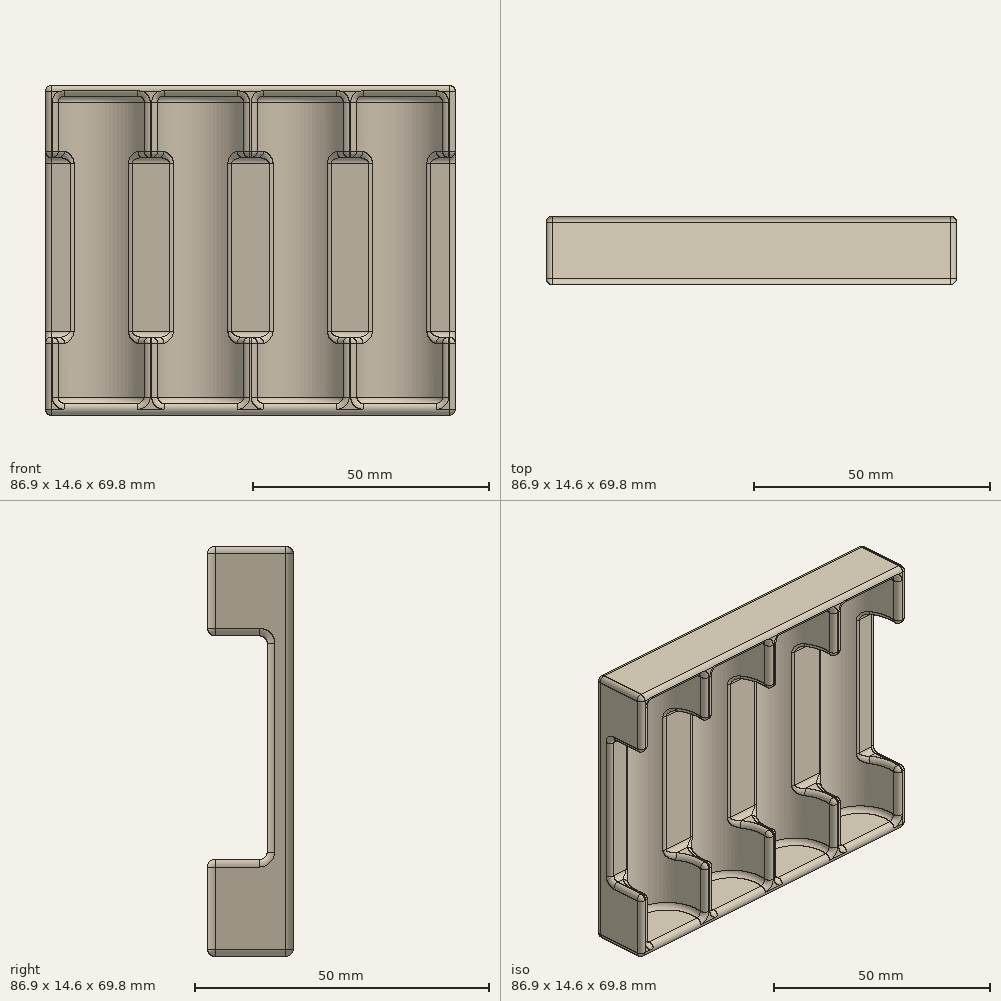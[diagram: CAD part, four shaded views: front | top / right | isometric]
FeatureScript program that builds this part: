
annotation { "Feature Type Name" : "Feature", "Feature Type Description" : "" }
export const myFeature = defineFeature(function(context is Context, id is Id, definition is map)
    precondition{}
    {
        {
            var Q0;
            Q0=qCreatedBy(makeId("Front.planeOp"),FACE);
            var sketch = newSketch(context, id + "F0", { "sketchPlane" : qUnion([Q0])});
            skLineSegment(sketch, "E0.bottom", {"start": v(0, 0) * mm, "end": v(86.87, 0) * mm});
            skLineSegment(sketch, "E0.top", {"start": v(0, 69.85) * mm, "end": v(86.87, 69.85) * mm});
            skLineSegment(sketch, "E0.left", {"start": v(0, 0) * mm, "end": v(0, 69.85) * mm});
            skLineSegment(sketch, "E0.right", {"start": v(86.87, 0) * mm, "end": v(86.87, 69.85) * mm});
            skSolve(sketch);
        }
        {
            var Q0;
            Q0=makeQuery(id+"F0.imprint","IMPRINT",FACE,{"disambiguationData":[TD([[makeQuery(id+"F0.imprint","IMPRINT",EDGE,{"derivedFrom":sQuery(id+"F0.wireOp",EDGE,"E0.bottom")}),1.0]])]});
            extrude(context, id + "F1", {"entities" : qUnion([Q0]), "depth" : 14.6 * mm});
        }
        {
            var Q0;
            Q0=makeQuery(id+"F1.opExtrude","SWEPT_FACE",FACE,{"disambiguationData":[OSD([sQuery(id+"F0.wireOp",EDGE,"E0.bottom")])]});
            var sketch = newSketch(context, id + "F2", { "sketchPlane" : qUnion([Q0])});
            skCircle(sketch, "E1", {"center": v(11.81, 11.43) * mm, "radius": 9.27 * mm});
            skCircle(sketch, "E2", {"center": v(32.9, 11.43) * mm, "radius": 9.27 * mm});
            skCircle(sketch, "E3", {"center": v(53.98, 11.43) * mm, "radius": 9.27 * mm});
            skCircle(sketch, "E4", {"center": v(75.06, 11.43) * mm, "radius": 9.27 * mm});
            skLineSegment(sketch, "E5", {"start": v(11.81, 11.43) * mm, "end": v(75.06, 11.43) * mm, "construction": true});
            skSolve(sketch);
        }
        {
            var Q0;
            {var subQ0=sQuery(id+"F2.wireOp",EDGE,"E1");var subQ1=makeQuery(id+"F1.opExtrude","CAP_EDGE",EDGE,{"disambiguationData":[OSD([sQuery(id+"F0.wireOp",EDGE,"E0.bottom")])],"isStart":false});var subQ2=makeQuery(id+"F2.imprint","INTERSECT",VERTEX,{"disambiguationData":[OD(0.0)],"derivedFrom":[subQ1,subQ0]});Q0=makeQuery(id+"F2.imprint","IMPRINT",FACE,{"disambiguationData":[TD([[makeQuery(id+"F2.imprint","IMPRINT",EDGE,{"disambiguationData":[TD([[subQ2,-1.0]])],"derivedFrom":subQ0}),1.0]])]});}
            var Q1;
            {var subQ0=sQuery(id+"F2.wireOp",EDGE,"E2");var subQ1=makeQuery(id+"F1.opExtrude","CAP_EDGE",EDGE,{"disambiguationData":[OSD([sQuery(id+"F0.wireOp",EDGE,"E0.bottom")])],"isStart":false});var subQ2=makeQuery(id+"F2.imprint","INTERSECT",VERTEX,{"disambiguationData":[OD(0.0)],"derivedFrom":[subQ1,subQ0]});Q1=makeQuery(id+"F2.imprint","IMPRINT",FACE,{"disambiguationData":[TD([[makeQuery(id+"F2.imprint","IMPRINT",EDGE,{"disambiguationData":[TD([[subQ2,-1.0]])],"derivedFrom":subQ0}),1.0]])]});}
            var Q2;
            {var subQ0=sQuery(id+"F2.wireOp",EDGE,"E3");var subQ1=makeQuery(id+"F1.opExtrude","CAP_EDGE",EDGE,{"disambiguationData":[OSD([sQuery(id+"F0.wireOp",EDGE,"E0.bottom")])],"isStart":false});var subQ2=makeQuery(id+"F2.imprint","INTERSECT",VERTEX,{"disambiguationData":[OD(0.0)],"derivedFrom":[subQ1,subQ0]});Q2=makeQuery(id+"F2.imprint","IMPRINT",FACE,{"disambiguationData":[TD([[makeQuery(id+"F2.imprint","IMPRINT",EDGE,{"disambiguationData":[TD([[subQ2,1.0]])],"derivedFrom":subQ0}),1.0]])]});}
            var Q3;
            {var subQ0=sQuery(id+"F2.wireOp",EDGE,"E4");var subQ1=makeQuery(id+"F1.opExtrude","CAP_EDGE",EDGE,{"disambiguationData":[OSD([sQuery(id+"F0.wireOp",EDGE,"E0.bottom")])],"isStart":false});var subQ2=makeQuery(id+"F2.imprint","INTERSECT",VERTEX,{"disambiguationData":[OD(0.0)],"derivedFrom":[subQ1,subQ0]});Q3=makeQuery(id+"F2.imprint","IMPRINT",FACE,{"disambiguationData":[TD([[makeQuery(id+"F2.imprint","IMPRINT",EDGE,{"disambiguationData":[TD([[subQ2,1.0]])],"derivedFrom":subQ0}),1.0]])]});}
            var Q4;
            Q4=sQuery(id+"F2.wireOp",EDGE,"E1");
            var Q5;
            Q5=sQuery(id+"F2.wireOp",EDGE,"E2");
            var Q6;
            Q6=sQuery(id+"F2.wireOp",EDGE,"E3");
            var Q7;
            Q7=sQuery(id+"F2.wireOp",EDGE,"E4");
            extrude(context, id + "F3", {"entities" : qUnion([Q0, Q1, Q2, Q3]), "operationType" : NewBodyOperationType.REMOVE, "surfaceEntities" : qUnion([Q4, Q5, Q6, Q7]), "oppositeDirection" : true, "depth" : 67.63 * mm, "hasSecondDirection" : true, "secondDirectionOppositeDirection" : true, "secondDirectionDepth" : 2.54 * mm});
        }
        {
            var Q0;
            Q0=makeQuery(id+"F1.opExtrude","CAP_FACE",FACE,{"disambiguationData":[OSD([sQuery(id+"F0.wireOp",EDGE,"E0.bottom"),sQuery(id+"F0.wireOp",EDGE,"E0.top"),sQuery(id+"F0.wireOp",EDGE,"E0.left"),sQuery(id+"F0.wireOp",EDGE,"E0.right")])],"isStart":false});
            var sketch = newSketch(context, id + "F4", { "sketchPlane" : qUnion([Q0])});
            skLineSegment(sketch, "E6.bottom", {"start": v(-1.4, 54.61) * mm, "end": v(92.29, 54.61) * mm});
            skLineSegment(sketch, "E6.top", {"start": v(-1.4, 16.51) * mm, "end": v(92.29, 16.51) * mm});
            skLineSegment(sketch, "E6.left", {"start": v(-1.4, 54.61) * mm, "end": v(-1.4, 16.51) * mm});
            skLineSegment(sketch, "E6.right", {"start": v(92.29, 54.61) * mm, "end": v(92.29, 16.51) * mm});
            skSolve(sketch);
        }
        {
            var Q0;
            Q0 = qSketchRegion(id + "F4", true);
            extrude(context, id + "F5", {"entities" : qUnion([Q0]), "operationType" : NewBodyOperationType.REMOVE, "oppositeDirection" : true, "depth" : 10.16 * mm});
        }
        {
            var Q0;
            {var subQ0=sQuery(id+"F2.wireOp",EDGE,"E3");var subQ1=sQuery(id+"F0.wireOp",EDGE,"E0.bottom");var subQ2=makeQuery(id+"F1.opExtrude","CAP_EDGE",EDGE,{"disambiguationData":[OSD([subQ1])],"isStart":false});Q0=makeQuery(id+"F3.boolean.opBoolean","COPY",EDGE,{"derivedFrom":makeQuery(id+"F3.opExtrude","CAP_EDGE",EDGE,{"disambiguationData":[OSD([subQ1]),TDD([makeQuery(id+"F2.imprint","IMPRINT",EDGE,{"disambiguationData":[TD([[makeQuery(id+"F2.imprint","INTERSECT",VERTEX,{"disambiguationData":[OD(0.0)],"derivedFrom":[subQ2,subQ0]}),1.0]])],"derivedFrom":subQ2})])],"isStart":false})});}
            var Q1;
            Q1=makeQuery(id+"F5.boolean.opBoolean","COPY",FACE,{"disambiguationData":[OD(4.0)],"derivedFrom":makeQuery(id+"F5.opExtrude","SWEPT_FACE",FACE,{"disambiguationData":[OSD([sQuery(id+"F4.wireOp",EDGE,"E6.top")])]})});
            var Q2;
            Q2=makeQuery(id+"F5.boolean.opBoolean","COPY",FACE,{"disambiguationData":[OD(3.0)],"derivedFrom":makeQuery(id+"F5.opExtrude","CAP_FACE",FACE,{"disambiguationData":[OSD([sQuery(id+"F4.wireOp",EDGE,"E6.bottom"),sQuery(id+"F4.wireOp",EDGE,"E6.top"),sQuery(id+"F4.wireOp",EDGE,"E6.left"),sQuery(id+"F4.wireOp",EDGE,"E6.right")])],"isStart":false})});
            var Q3;
            Q3=makeQuery(id+"F3.boolean.opBoolean","COPY",FACE,{"derivedFrom":makeQuery(id+"F3.opExtrude","CAP_FACE",FACE,{"disambiguationData":[OSD([sQuery(id+"F0.wireOp",EDGE,"E0.bottom"),sQuery(id+"F2.wireOp",EDGE,"E4")])],"isStart":false})});
            var Q4;
            Q4=makeQuery(id+"F5.boolean.opBoolean","COPY",FACE,{"disambiguationData":[OD(3.0)],"derivedFrom":makeQuery(id+"F5.opExtrude","SWEPT_FACE",FACE,{"disambiguationData":[OSD([sQuery(id+"F4.wireOp",EDGE,"E6.top")])]})});
            var Q5;
            Q5=makeQuery(id+"F5.boolean.opBoolean","INTERSECT",EDGE,{"derivedFrom":[makeQuery(id+"F1.opExtrude","SWEPT_FACE",FACE,{"disambiguationData":[OSD([sQuery(id+"F0.wireOp",EDGE,"E0.left")])]}),makeQuery(id+"F5.opExtrude","CAP_FACE",FACE,{"disambiguationData":[OSD([sQuery(id+"F4.wireOp",EDGE,"E6.bottom"),sQuery(id+"F4.wireOp",EDGE,"E6.top"),sQuery(id+"F4.wireOp",EDGE,"E6.left"),sQuery(id+"F4.wireOp",EDGE,"E6.right")])],"isStart":false})]});
            var Q6;
            Q6=makeQuery(id+"F5.boolean.opBoolean","COPY",FACE,{"disambiguationData":[OD(4.0)],"derivedFrom":makeQuery(id+"F5.opExtrude","CAP_FACE",FACE,{"disambiguationData":[OSD([sQuery(id+"F4.wireOp",EDGE,"E6.bottom"),sQuery(id+"F4.wireOp",EDGE,"E6.top"),sQuery(id+"F4.wireOp",EDGE,"E6.left"),sQuery(id+"F4.wireOp",EDGE,"E6.right")])],"isStart":false})});
            var Q7;
            Q7=makeQuery(id+"F5.boolean.opBoolean","COPY",FACE,{"disambiguationData":[OD(0.0)],"derivedFrom":makeQuery(id+"F5.opExtrude","SWEPT_FACE",FACE,{"disambiguationData":[OSD([sQuery(id+"F4.wireOp",EDGE,"E6.top")])]})});
            var Q8;
            Q8=makeQuery(id+"F5.boolean.opBoolean","INTERSECT",EDGE,{"derivedFrom":[makeQuery(id+"F1.opExtrude","SWEPT_FACE",FACE,{"disambiguationData":[OSD([sQuery(id+"F0.wireOp",EDGE,"E0.left")])]}),makeQuery(id+"F5.opExtrude","SWEPT_FACE",FACE,{"disambiguationData":[OSD([sQuery(id+"F4.wireOp",EDGE,"E6.top")])]})]});
            var Q9;
            Q9=makeQuery(id+"F5.boolean.opBoolean","COPY",FACE,{"disambiguationData":[OD(2.0)],"derivedFrom":makeQuery(id+"F5.opExtrude","CAP_FACE",FACE,{"disambiguationData":[OSD([sQuery(id+"F4.wireOp",EDGE,"E6.bottom"),sQuery(id+"F4.wireOp",EDGE,"E6.top"),sQuery(id+"F4.wireOp",EDGE,"E6.left"),sQuery(id+"F4.wireOp",EDGE,"E6.right")])],"isStart":false})});
            var Q10;
            Q10=makeQuery(id+"F5.boolean.opBoolean","COPY",FACE,{"disambiguationData":[OD(0.0)],"derivedFrom":makeQuery(id+"F5.opExtrude","CAP_FACE",FACE,{"disambiguationData":[OSD([sQuery(id+"F4.wireOp",EDGE,"E6.bottom"),sQuery(id+"F4.wireOp",EDGE,"E6.top"),sQuery(id+"F4.wireOp",EDGE,"E6.left"),sQuery(id+"F4.wireOp",EDGE,"E6.right")])],"isStart":false})});
            var Q11;
            Q11=makeQuery(id+"F5.boolean.opBoolean","COPY",FACE,{"disambiguationData":[OD(1.0)],"derivedFrom":makeQuery(id+"F5.opExtrude","CAP_FACE",FACE,{"disambiguationData":[OSD([sQuery(id+"F4.wireOp",EDGE,"E6.bottom"),sQuery(id+"F4.wireOp",EDGE,"E6.top"),sQuery(id+"F4.wireOp",EDGE,"E6.left"),sQuery(id+"F4.wireOp",EDGE,"E6.right")])],"isStart":false})});
            var Q12;
            Q12=makeQuery(id+"F1.opExtrude","SWEPT_FACE",FACE,{"disambiguationData":[OSD([sQuery(id+"F0.wireOp",EDGE,"E0.left")])]});
            var Q13;
            Q13=makeQuery(id+"F1.opExtrude","SWEPT_FACE",FACE,{"disambiguationData":[OSD([sQuery(id+"F0.wireOp",EDGE,"E0.right")])]});
            var Q14;
            Q14=makeQuery(id+"F3.boolean.opBoolean","COPY",FACE,{"derivedFrom":makeQuery(id+"F3.opExtrude","SWEPT_FACE",FACE,{"disambiguationData":[OSD([sQuery(id+"F2.wireOp",EDGE,"E1")])]})});
            var Q15;
            Q15=makeQuery(id+"F3.boolean.opBoolean","COPY",FACE,{"derivedFrom":makeQuery(id+"F3.opExtrude","SWEPT_FACE",FACE,{"disambiguationData":[OSD([sQuery(id+"F2.wireOp",EDGE,"E2")])]})});
            var Q16;
            Q16=makeQuery(id+"F3.boolean.opBoolean","COPY",FACE,{"derivedFrom":makeQuery(id+"F3.opExtrude","SWEPT_FACE",FACE,{"disambiguationData":[OSD([sQuery(id+"F2.wireOp",EDGE,"E3")])]})});
            var Q17;
            Q17=makeQuery(id+"F3.boolean.opBoolean","COPY",FACE,{"derivedFrom":makeQuery(id+"F3.opExtrude","SWEPT_FACE",FACE,{"disambiguationData":[OSD([sQuery(id+"F2.wireOp",EDGE,"E4")])]})});
            var Q18;
            {var subQ1=sQuery(id+"F0.wireOp",EDGE,"E0.bottom");var subQ4=sQuery(id+"F0.wireOp",EDGE,"E0.left");var subQ6=sQuery(id+"F0.wireOp",EDGE,"E0.right");Q18=makeQuery(id+"F5.boolean.opBoolean","SPLIT",FACE,{"disambiguationData":[TD([makeQuery(id+"F1.opExtrude","SWEPT_FACE",FACE,{"disambiguationData":[OSD([subQ1])]})])],"derivedFrom":makeQuery(id+"F1.opExtrude","CAP_FACE",FACE,{"disambiguationData":[OSD([subQ1,sQuery(id+"F0.wireOp",EDGE,"E0.top"),subQ4,subQ6])],"isStart":false})});}
            var Q19;
            Q19=makeQuery(id+"F5.boolean.opBoolean","COPY",FACE,{"disambiguationData":[OD(1.0)],"derivedFrom":makeQuery(id+"F5.opExtrude","SWEPT_FACE",FACE,{"disambiguationData":[OSD([sQuery(id+"F4.wireOp",EDGE,"E6.top")])]})});
            var Q20;
            {var subQ2=sQuery(id+"F0.wireOp",EDGE,"E0.bottom");var subQ4=sQuery(id+"F0.wireOp",EDGE,"E0.top");var subQ5=sQuery(id+"F0.wireOp",EDGE,"E0.left");var subQ7=sQuery(id+"F0.wireOp",EDGE,"E0.right");Q20=makeQuery(id+"F5.boolean.opBoolean","SPLIT",FACE,{"disambiguationData":[TD([makeQuery(id+"F1.opExtrude","SWEPT_FACE",FACE,{"disambiguationData":[OSD([subQ4])]})])],"derivedFrom":makeQuery(id+"F1.opExtrude","CAP_FACE",FACE,{"disambiguationData":[OSD([subQ2,subQ4,subQ5,subQ7])],"isStart":false})});}
            var Q21;
            Q21=makeQuery(id+"F5.boolean.opBoolean","COPY",FACE,{"disambiguationData":[OD(1.0)],"derivedFrom":makeQuery(id+"F5.opExtrude","SWEPT_FACE",FACE,{"disambiguationData":[OSD([sQuery(id+"F4.wireOp",EDGE,"E6.bottom")])]})});
            var Q22;
            Q22=makeQuery(id+"F5.boolean.opBoolean","COPY",FACE,{"disambiguationData":[OD(3.0)],"derivedFrom":makeQuery(id+"F5.opExtrude","SWEPT_FACE",FACE,{"disambiguationData":[OSD([sQuery(id+"F4.wireOp",EDGE,"E6.bottom")])]})});
            var Q23;
            Q23=makeQuery(id+"F5.boolean.opBoolean","COPY",EDGE,{"disambiguationData":[OD(2.0)],"derivedFrom":makeQuery(id+"F5.opExtrude","CAP_EDGE",EDGE,{"disambiguationData":[OSD([sQuery(id+"F4.wireOp",EDGE,"E6.top")])],"isStart":false})});
            var Q24;
            Q24=makeQuery(id+"F3.boolean.opBoolean","COPY",FACE,{"derivedFrom":makeQuery(id+"F3.opExtrude","CAP_FACE",FACE,{"disambiguationData":[OSD([sQuery(id+"F0.wireOp",EDGE,"E0.bottom"),sQuery(id+"F2.wireOp",EDGE,"E4")])],"isStart":true})});
            var Q25;
            Q25=makeQuery(id+"F3.boolean.opBoolean","COPY",FACE,{"derivedFrom":makeQuery(id+"F3.opExtrude","CAP_FACE",FACE,{"disambiguationData":[OSD([sQuery(id+"F0.wireOp",EDGE,"E0.bottom"),sQuery(id+"F2.wireOp",EDGE,"E3")])],"isStart":false})});
            var Q26;
            Q26=makeQuery(id+"F3.boolean.opBoolean","COPY",FACE,{"derivedFrom":makeQuery(id+"F3.opExtrude","CAP_FACE",FACE,{"disambiguationData":[OSD([sQuery(id+"F0.wireOp",EDGE,"E0.bottom"),sQuery(id+"F2.wireOp",EDGE,"E3")])],"isStart":true})});
            var Q27;
            Q27=makeQuery(id+"F3.boolean.opBoolean","COPY",FACE,{"derivedFrom":makeQuery(id+"F3.opExtrude","CAP_FACE",FACE,{"disambiguationData":[OSD([sQuery(id+"F0.wireOp",EDGE,"E0.bottom"),sQuery(id+"F2.wireOp",EDGE,"E2")])],"isStart":false})});
            var Q28;
            Q28=makeQuery(id+"F3.boolean.opBoolean","COPY",FACE,{"derivedFrom":makeQuery(id+"F3.opExtrude","CAP_FACE",FACE,{"disambiguationData":[OSD([sQuery(id+"F0.wireOp",EDGE,"E0.bottom"),sQuery(id+"F2.wireOp",EDGE,"E2")])],"isStart":true})});
            var Q29;
            Q29=makeQuery(id+"F3.boolean.opBoolean","COPY",FACE,{"derivedFrom":makeQuery(id+"F3.opExtrude","CAP_FACE",FACE,{"disambiguationData":[OSD([sQuery(id+"F0.wireOp",EDGE,"E0.bottom"),sQuery(id+"F2.wireOp",EDGE,"E1")])],"isStart":false})});
            var Q30;
            Q30=makeQuery(id+"F5.boolean.opBoolean","COPY",FACE,{"disambiguationData":[OD(2.0)],"derivedFrom":makeQuery(id+"F5.opExtrude","SWEPT_FACE",FACE,{"disambiguationData":[OSD([sQuery(id+"F4.wireOp",EDGE,"E6.top")])]})});
            var Q31;
            Q31=makeQuery(id+"F1.opExtrude","CAP_EDGE",EDGE,{"disambiguationData":[OSD([sQuery(id+"F0.wireOp",EDGE,"E0.top")])],"isStart":false});
            var Q32;
            Q32=makeQuery(id+"F1.opExtrude","CAP_EDGE",EDGE,{"disambiguationData":[OSD([sQuery(id+"F0.wireOp",EDGE,"E0.top")])],"isStart":true});
            var Q33;
            Q33=makeQuery(id+"F1.opExtrude","CAP_EDGE",EDGE,{"disambiguationData":[OSD([sQuery(id+"F0.wireOp",EDGE,"E0.bottom")])],"isStart":false});
            var Q34;
            Q34=makeQuery(id+"F1.opExtrude","SWEPT_FACE",FACE,{"disambiguationData":[OSD([sQuery(id+"F0.wireOp",EDGE,"E0.top")])]});
            var Q35;
            Q35=makeQuery(id+"F1.opExtrude","SWEPT_EDGE",EDGE,{"disambiguationData":[OSD([sQuery(id+"F0.wireOp",EDGE,"E0.top"),sQuery(id+"F0.wireOp",EDGE,"E0.right")])]});
            var Q36;
            Q36=makeQuery(id+"F1.opExtrude","SWEPT_EDGE",EDGE,{"disambiguationData":[OSD([sQuery(id+"F0.wireOp",EDGE,"E0.top"),sQuery(id+"F0.wireOp",EDGE,"E0.left")])]});
            var Q37;
            Q37=makeQuery(id+"F1.opExtrude","SWEPT_EDGE",EDGE,{"disambiguationData":[OSD([sQuery(id+"F0.wireOp",EDGE,"E0.bottom"),sQuery(id+"F0.wireOp",EDGE,"E0.right")])]});
            var Q38;
            Q38=makeQuery(id+"F1.opExtrude","CAP_FACE",FACE,{"disambiguationData":[OSD([sQuery(id+"F0.wireOp",EDGE,"E0.bottom"),sQuery(id+"F0.wireOp",EDGE,"E0.top"),sQuery(id+"F0.wireOp",EDGE,"E0.left"),sQuery(id+"F0.wireOp",EDGE,"E0.right")])],"isStart":true});
            var Q39;
            {var subQ0=sQuery(id+"F2.wireOp",EDGE,"E2");var subQ1=sQuery(id+"F0.wireOp",EDGE,"E0.bottom");var subQ2=makeQuery(id+"F1.opExtrude","CAP_EDGE",EDGE,{"disambiguationData":[OSD([subQ1])],"isStart":false});Q39=makeQuery(id+"F3.boolean.opBoolean","COPY",EDGE,{"derivedFrom":makeQuery(id+"F3.opExtrude","CAP_EDGE",EDGE,{"disambiguationData":[OSD([subQ1]),TDD([makeQuery(id+"F2.imprint","IMPRINT",EDGE,{"disambiguationData":[TD([[makeQuery(id+"F2.imprint","INTERSECT",VERTEX,{"disambiguationData":[OD(0.0)],"derivedFrom":[subQ2,subQ0]}),-1.0]])],"derivedFrom":subQ2})])],"isStart":true})});}
            var Q40;
            Q40=makeQuery(id+"F1.opExtrude","SWEPT_FACE",FACE,{"disambiguationData":[OSD([sQuery(id+"F0.wireOp",EDGE,"E0.bottom")])]});
            var Q41;
            Q41=makeQuery(id+"F5.boolean.opBoolean","COPY",EDGE,{"disambiguationData":[OD(1.0)],"derivedFrom":makeQuery(id+"F5.opExtrude","CAP_EDGE",EDGE,{"disambiguationData":[OSD([sQuery(id+"F4.wireOp",EDGE,"E6.top")])],"isStart":true})});
            var Q42;
            Q42=makeQuery(id+"F5.boolean.opBoolean","COPY",EDGE,{"disambiguationData":[OD(3.0)],"derivedFrom":makeQuery(id+"F5.opExtrude","CAP_EDGE",EDGE,{"disambiguationData":[OSD([sQuery(id+"F4.wireOp",EDGE,"E6.top")])],"isStart":false})});
            var Q43;
            Q43=makeQuery(id+"F5.boolean.opBoolean","INTERSECT",EDGE,{"disambiguationData":[OD(0.0)],"derivedFrom":[makeQuery(id+"F3.boolean.opBoolean","COPY",FACE,{"derivedFrom":makeQuery(id+"F3.opExtrude","SWEPT_FACE",FACE,{"disambiguationData":[OSD([sQuery(id+"F2.wireOp",EDGE,"E2")])]})}),makeQuery(id+"F5.opExtrude","SWEPT_FACE",FACE,{"disambiguationData":[OSD([sQuery(id+"F4.wireOp",EDGE,"E6.top")])]})]});
            var Q44;
            Q44=makeQuery(id+"F5.boolean.opBoolean","INTERSECT",EDGE,{"derivedFrom":[makeQuery(id+"F1.opExtrude","SWEPT_FACE",FACE,{"disambiguationData":[OSD([sQuery(id+"F0.wireOp",EDGE,"E0.left")])]}),makeQuery(id+"F5.opExtrude","SWEPT_FACE",FACE,{"disambiguationData":[OSD([sQuery(id+"F4.wireOp",EDGE,"E6.bottom")])]})]});
            var Q45;
            Q45=makeQuery(id+"F5.boolean.opBoolean","INTERSECT",EDGE,{"disambiguationData":[OD(1.0)],"derivedFrom":[makeQuery(id+"F3.boolean.opBoolean","COPY",FACE,{"derivedFrom":makeQuery(id+"F3.opExtrude","SWEPT_FACE",FACE,{"disambiguationData":[OSD([sQuery(id+"F2.wireOp",EDGE,"E1")])]})}),makeQuery(id+"F5.opExtrude","CAP_FACE",FACE,{"disambiguationData":[OSD([sQuery(id+"F4.wireOp",EDGE,"E6.bottom"),sQuery(id+"F4.wireOp",EDGE,"E6.top"),sQuery(id+"F4.wireOp",EDGE,"E6.left"),sQuery(id+"F4.wireOp",EDGE,"E6.right")])],"isStart":false})]});
            var Q46;
            Q46=makeQuery(id+"F3.boolean.opBoolean","COPY",EDGE,{"derivedFrom":makeQuery(id+"F3.opExtrude","CAP_EDGE",EDGE,{"disambiguationData":[OSD([sQuery(id+"F2.wireOp",EDGE,"E3")])],"isStart":true})});
            var Q47;
            Q47=makeQuery(id+"F3.boolean.opBoolean","COPY",EDGE,{"derivedFrom":makeQuery(id+"F3.opExtrude","CAP_EDGE",EDGE,{"disambiguationData":[OSD([sQuery(id+"F2.wireOp",EDGE,"E2")])],"isStart":false})});
            var Q48;
            Q48=makeQuery(id+"F5.boolean.opBoolean","INTERSECT",EDGE,{"derivedFrom":[makeQuery(id+"F1.opExtrude","SWEPT_FACE",FACE,{"disambiguationData":[OSD([sQuery(id+"F0.wireOp",EDGE,"E0.right")])]}),makeQuery(id+"F5.opExtrude","SWEPT_FACE",FACE,{"disambiguationData":[OSD([sQuery(id+"F4.wireOp",EDGE,"E6.bottom")])]})]});
            var Q49;
            Q49=makeQuery(id+"F5.boolean.opBoolean","INTERSECT",EDGE,{"disambiguationData":[OD(1.0)],"derivedFrom":[makeQuery(id+"F3.boolean.opBoolean","COPY",FACE,{"derivedFrom":makeQuery(id+"F3.opExtrude","SWEPT_FACE",FACE,{"disambiguationData":[OSD([sQuery(id+"F2.wireOp",EDGE,"E4")])]})}),makeQuery(id+"F5.opExtrude","SWEPT_FACE",FACE,{"disambiguationData":[OSD([sQuery(id+"F4.wireOp",EDGE,"E6.top")])]})]});
            var Q50;
            Q50=makeQuery(id+"F5.boolean.opBoolean","INTERSECT",EDGE,{"disambiguationData":[OD(1.0)],"derivedFrom":[makeQuery(id+"F3.boolean.opBoolean","COPY",FACE,{"derivedFrom":makeQuery(id+"F3.opExtrude","SWEPT_FACE",FACE,{"disambiguationData":[OSD([sQuery(id+"F2.wireOp",EDGE,"E2")])]})}),makeQuery(id+"F5.opExtrude","SWEPT_FACE",FACE,{"disambiguationData":[OSD([sQuery(id+"F4.wireOp",EDGE,"E6.bottom")])]})]});
            var Q51;
            {var subQ0=sQuery(id+"F0.wireOp",EDGE,"E0.bottom");var subQ1=sQuery(id+"F2.wireOp",EDGE,"E3");Q51=makeQuery(id+"F5.boolean.opBoolean","SPLIT",EDGE,{"disambiguationData":[TD([makeQuery(id+"F5.opExtrude","SWEPT_FACE",FACE,{"disambiguationData":[OSD([sQuery(id+"F4.wireOp",EDGE,"E6.bottom")])]})])],"derivedFrom":makeQuery(id+"F3.boolean.opBoolean","COPY",EDGE,{"derivedFrom":makeQuery(id+"F3.opExtrude","SWEPT_EDGE",EDGE,{"disambiguationData":[OSD([subQ0,subQ1]),TDD([makeQuery(id+"F2.imprint","INTERSECT",VERTEX,{"disambiguationData":[OD(0.0)],"derivedFrom":[makeQuery(id+"F1.opExtrude","CAP_EDGE",EDGE,{"disambiguationData":[OSD([subQ0])],"isStart":false}),subQ1]})])]})})});}
            var Q52;
            Q52=makeQuery(id+"F5.boolean.opBoolean","COPY",EDGE,{"disambiguationData":[OD(0.0)],"derivedFrom":makeQuery(id+"F5.opExtrude","CAP_EDGE",EDGE,{"disambiguationData":[OSD([sQuery(id+"F4.wireOp",EDGE,"E6.top")])],"isStart":false})});
            var Q53;
            Q53=makeQuery(id+"F5.boolean.opBoolean","INTERSECT",EDGE,{"disambiguationData":[OD(0.0)],"derivedFrom":[makeQuery(id+"F3.boolean.opBoolean","COPY",FACE,{"derivedFrom":makeQuery(id+"F3.opExtrude","SWEPT_FACE",FACE,{"disambiguationData":[OSD([sQuery(id+"F2.wireOp",EDGE,"E1")])]})}),makeQuery(id+"F5.opExtrude","CAP_FACE",FACE,{"disambiguationData":[OSD([sQuery(id+"F4.wireOp",EDGE,"E6.bottom"),sQuery(id+"F4.wireOp",EDGE,"E6.top"),sQuery(id+"F4.wireOp",EDGE,"E6.left"),sQuery(id+"F4.wireOp",EDGE,"E6.right")])],"isStart":false})]});
            var Q54;
            Q54=makeQuery(id+"F5.boolean.opBoolean","COPY",EDGE,{"disambiguationData":[OD(0.0)],"derivedFrom":makeQuery(id+"F5.opExtrude","CAP_EDGE",EDGE,{"disambiguationData":[OSD([sQuery(id+"F4.wireOp",EDGE,"E6.top")])],"isStart":true})});
            var Q55;
            Q55=makeQuery(id+"F5.boolean.opBoolean","INTERSECT",EDGE,{"disambiguationData":[OD(0.0)],"derivedFrom":[makeQuery(id+"F3.boolean.opBoolean","COPY",FACE,{"derivedFrom":makeQuery(id+"F3.opExtrude","SWEPT_FACE",FACE,{"disambiguationData":[OSD([sQuery(id+"F2.wireOp",EDGE,"E4")])]})}),makeQuery(id+"F5.opExtrude","SWEPT_FACE",FACE,{"disambiguationData":[OSD([sQuery(id+"F4.wireOp",EDGE,"E6.bottom")])]})]});
            var Q56;
            Q56=makeQuery(id+"F5.boolean.opBoolean","INTERSECT",EDGE,{"derivedFrom":[makeQuery(id+"F1.opExtrude","SWEPT_FACE",FACE,{"disambiguationData":[OSD([sQuery(id+"F0.wireOp",EDGE,"E0.right")])]}),makeQuery(id+"F5.opExtrude","CAP_FACE",FACE,{"disambiguationData":[OSD([sQuery(id+"F4.wireOp",EDGE,"E6.bottom"),sQuery(id+"F4.wireOp",EDGE,"E6.top"),sQuery(id+"F4.wireOp",EDGE,"E6.left"),sQuery(id+"F4.wireOp",EDGE,"E6.right")])],"isStart":false})]});
            var Q57;
            Q57=makeQuery(id+"F5.boolean.opBoolean","INTERSECT",EDGE,{"disambiguationData":[OD(0.0)],"derivedFrom":[makeQuery(id+"F3.boolean.opBoolean","COPY",FACE,{"derivedFrom":makeQuery(id+"F3.opExtrude","SWEPT_FACE",FACE,{"disambiguationData":[OSD([sQuery(id+"F2.wireOp",EDGE,"E4")])]})}),makeQuery(id+"F5.opExtrude","CAP_FACE",FACE,{"disambiguationData":[OSD([sQuery(id+"F4.wireOp",EDGE,"E6.bottom"),sQuery(id+"F4.wireOp",EDGE,"E6.top"),sQuery(id+"F4.wireOp",EDGE,"E6.left"),sQuery(id+"F4.wireOp",EDGE,"E6.right")])],"isStart":false})]});
            var Q58;
            Q58=makeQuery(id+"F5.boolean.opBoolean","COPY",EDGE,{"disambiguationData":[OD(3.0)],"derivedFrom":makeQuery(id+"F5.opExtrude","CAP_EDGE",EDGE,{"disambiguationData":[OSD([sQuery(id+"F4.wireOp",EDGE,"E6.bottom")])],"isStart":true})});
            var Q59;
            Q59=makeQuery(id+"F5.boolean.opBoolean","INTERSECT",EDGE,{"disambiguationData":[OD(1.0)],"derivedFrom":[makeQuery(id+"F3.boolean.opBoolean","COPY",FACE,{"derivedFrom":makeQuery(id+"F3.opExtrude","SWEPT_FACE",FACE,{"disambiguationData":[OSD([sQuery(id+"F2.wireOp",EDGE,"E2")])]})}),makeQuery(id+"F5.opExtrude","SWEPT_FACE",FACE,{"disambiguationData":[OSD([sQuery(id+"F4.wireOp",EDGE,"E6.top")])]})]});
            var Q60;
            Q60=makeQuery(id+"F5.boolean.opBoolean","INTERSECT",EDGE,{"disambiguationData":[OD(0.0)],"derivedFrom":[makeQuery(id+"F3.boolean.opBoolean","COPY",FACE,{"derivedFrom":makeQuery(id+"F3.opExtrude","SWEPT_FACE",FACE,{"disambiguationData":[OSD([sQuery(id+"F2.wireOp",EDGE,"E1")])]})}),makeQuery(id+"F5.opExtrude","SWEPT_FACE",FACE,{"disambiguationData":[OSD([sQuery(id+"F4.wireOp",EDGE,"E6.top")])]})]});
            var Q61;
            Q61=makeQuery(id+"F5.boolean.opBoolean","COPY",EDGE,{"disambiguationData":[OD(4.0)],"derivedFrom":makeQuery(id+"F5.opExtrude","CAP_EDGE",EDGE,{"disambiguationData":[OSD([sQuery(id+"F4.wireOp",EDGE,"E6.top")])],"isStart":false})});
            var Q62;
            Q62=makeQuery(id+"F5.boolean.opBoolean","COPY",EDGE,{"disambiguationData":[OD(2.0)],"derivedFrom":makeQuery(id+"F5.opExtrude","CAP_EDGE",EDGE,{"disambiguationData":[OSD([sQuery(id+"F4.wireOp",EDGE,"E6.top")])],"isStart":true})});
            var Q63;
            Q63=makeQuery(id+"F5.boolean.opBoolean","COPY",EDGE,{"disambiguationData":[OD(1.0)],"derivedFrom":makeQuery(id+"F5.opExtrude","CAP_EDGE",EDGE,{"disambiguationData":[OSD([sQuery(id+"F4.wireOp",EDGE,"E6.bottom")])],"isStart":false})});
            var Q64;
            Q64=makeQuery(id+"F5.boolean.opBoolean","INTERSECT",EDGE,{"disambiguationData":[OD(0.0)],"derivedFrom":[makeQuery(id+"F3.boolean.opBoolean","COPY",FACE,{"derivedFrom":makeQuery(id+"F3.opExtrude","SWEPT_FACE",FACE,{"disambiguationData":[OSD([sQuery(id+"F2.wireOp",EDGE,"E3")])]})}),makeQuery(id+"F5.opExtrude","CAP_FACE",FACE,{"disambiguationData":[OSD([sQuery(id+"F4.wireOp",EDGE,"E6.bottom"),sQuery(id+"F4.wireOp",EDGE,"E6.top"),sQuery(id+"F4.wireOp",EDGE,"E6.left"),sQuery(id+"F4.wireOp",EDGE,"E6.right")])],"isStart":false})]});
            var Q65;
            Q65=makeQuery(id+"F5.boolean.opBoolean","INTERSECT",EDGE,{"derivedFrom":[makeQuery(id+"F1.opExtrude","SWEPT_FACE",FACE,{"disambiguationData":[OSD([sQuery(id+"F0.wireOp",EDGE,"E0.right")])]}),makeQuery(id+"F5.opExtrude","SWEPT_FACE",FACE,{"disambiguationData":[OSD([sQuery(id+"F4.wireOp",EDGE,"E6.top")])]})]});
            var Q66;
            Q66=makeQuery(id+"F5.boolean.opBoolean","COPY",EDGE,{"disambiguationData":[OD(1.0)],"derivedFrom":makeQuery(id+"F5.opExtrude","CAP_EDGE",EDGE,{"disambiguationData":[OSD([sQuery(id+"F4.wireOp",EDGE,"E6.top")])],"isStart":false})});
            var Q67;
            Q67=makeQuery(id+"F5.boolean.opBoolean","COPY",EDGE,{"disambiguationData":[OD(2.0)],"derivedFrom":makeQuery(id+"F5.opExtrude","CAP_EDGE",EDGE,{"disambiguationData":[OSD([sQuery(id+"F4.wireOp",EDGE,"E6.bottom")])],"isStart":false})});
            var Q68;
            Q68=makeQuery(id+"F5.boolean.opBoolean","INTERSECT",EDGE,{"disambiguationData":[OD(1.0)],"derivedFrom":[makeQuery(id+"F3.boolean.opBoolean","COPY",FACE,{"derivedFrom":makeQuery(id+"F3.opExtrude","SWEPT_FACE",FACE,{"disambiguationData":[OSD([sQuery(id+"F2.wireOp",EDGE,"E3")])]})}),makeQuery(id+"F5.opExtrude","CAP_FACE",FACE,{"disambiguationData":[OSD([sQuery(id+"F4.wireOp",EDGE,"E6.bottom"),sQuery(id+"F4.wireOp",EDGE,"E6.top"),sQuery(id+"F4.wireOp",EDGE,"E6.left"),sQuery(id+"F4.wireOp",EDGE,"E6.right")])],"isStart":false})]});
            var Q69;
            Q69=makeQuery(id+"F5.boolean.opBoolean","INTERSECT",EDGE,{"disambiguationData":[OD(1.0)],"derivedFrom":[makeQuery(id+"F3.boolean.opBoolean","COPY",FACE,{"derivedFrom":makeQuery(id+"F3.opExtrude","SWEPT_FACE",FACE,{"disambiguationData":[OSD([sQuery(id+"F2.wireOp",EDGE,"E4")])]})}),makeQuery(id+"F5.opExtrude","CAP_FACE",FACE,{"disambiguationData":[OSD([sQuery(id+"F4.wireOp",EDGE,"E6.bottom"),sQuery(id+"F4.wireOp",EDGE,"E6.top"),sQuery(id+"F4.wireOp",EDGE,"E6.left"),sQuery(id+"F4.wireOp",EDGE,"E6.right")])],"isStart":false})]});
            var Q70;
            Q70=makeQuery(id+"F5.boolean.opBoolean","INTERSECT",EDGE,{"disambiguationData":[OD(1.0)],"derivedFrom":[makeQuery(id+"F3.boolean.opBoolean","COPY",FACE,{"derivedFrom":makeQuery(id+"F3.opExtrude","SWEPT_FACE",FACE,{"disambiguationData":[OSD([sQuery(id+"F2.wireOp",EDGE,"E1")])]})}),makeQuery(id+"F5.opExtrude","SWEPT_FACE",FACE,{"disambiguationData":[OSD([sQuery(id+"F4.wireOp",EDGE,"E6.top")])]})]});
            var Q71;
            Q71=makeQuery(id+"F5.boolean.opBoolean","INTERSECT",EDGE,{"disambiguationData":[OD(0.0)],"derivedFrom":[makeQuery(id+"F3.boolean.opBoolean","COPY",FACE,{"derivedFrom":makeQuery(id+"F3.opExtrude","SWEPT_FACE",FACE,{"disambiguationData":[OSD([sQuery(id+"F2.wireOp",EDGE,"E3")])]})}),makeQuery(id+"F5.opExtrude","SWEPT_FACE",FACE,{"disambiguationData":[OSD([sQuery(id+"F4.wireOp",EDGE,"E6.bottom")])]})]});
            var Q72;
            Q72=makeQuery(id+"F5.boolean.opBoolean","COPY",EDGE,{"disambiguationData":[OD(3.0)],"derivedFrom":makeQuery(id+"F5.opExtrude","CAP_EDGE",EDGE,{"disambiguationData":[OSD([sQuery(id+"F4.wireOp",EDGE,"E6.top")])],"isStart":true})});
            var Q73;
            Q73=makeQuery(id+"F5.boolean.opBoolean","INTERSECT",EDGE,{"disambiguationData":[OD(0.0)],"derivedFrom":[makeQuery(id+"F3.boolean.opBoolean","COPY",FACE,{"derivedFrom":makeQuery(id+"F3.opExtrude","SWEPT_FACE",FACE,{"disambiguationData":[OSD([sQuery(id+"F2.wireOp",EDGE,"E2")])]})}),makeQuery(id+"F5.opExtrude","CAP_FACE",FACE,{"disambiguationData":[OSD([sQuery(id+"F4.wireOp",EDGE,"E6.bottom"),sQuery(id+"F4.wireOp",EDGE,"E6.top"),sQuery(id+"F4.wireOp",EDGE,"E6.left"),sQuery(id+"F4.wireOp",EDGE,"E6.right")])],"isStart":false})]});
            var Q74;
            {var subQ0=sQuery(id+"F0.wireOp",EDGE,"E0.bottom");var subQ1=sQuery(id+"F2.wireOp",EDGE,"E3");Q74=makeQuery(id+"F5.boolean.opBoolean","SPLIT",EDGE,{"disambiguationData":[TD([makeQuery(id+"F5.opExtrude","SWEPT_FACE",FACE,{"disambiguationData":[OSD([sQuery(id+"F4.wireOp",EDGE,"E6.top")])]})])],"derivedFrom":makeQuery(id+"F3.boolean.opBoolean","COPY",EDGE,{"derivedFrom":makeQuery(id+"F3.opExtrude","SWEPT_EDGE",EDGE,{"disambiguationData":[OSD([subQ0,subQ1]),TDD([makeQuery(id+"F2.imprint","INTERSECT",VERTEX,{"disambiguationData":[OD(1.0)],"derivedFrom":[makeQuery(id+"F1.opExtrude","CAP_EDGE",EDGE,{"disambiguationData":[OSD([subQ0])],"isStart":false}),subQ1]})])]})})});}
            var Q75;
            {var subQ0=sQuery(id+"F0.wireOp",EDGE,"E0.bottom");var subQ1=sQuery(id+"F2.wireOp",EDGE,"E2");Q75=makeQuery(id+"F5.boolean.opBoolean","SPLIT",EDGE,{"disambiguationData":[TD([makeQuery(id+"F5.opExtrude","SWEPT_FACE",FACE,{"disambiguationData":[OSD([sQuery(id+"F4.wireOp",EDGE,"E6.bottom")])]})])],"derivedFrom":makeQuery(id+"F3.boolean.opBoolean","COPY",EDGE,{"derivedFrom":makeQuery(id+"F3.opExtrude","SWEPT_EDGE",EDGE,{"disambiguationData":[OSD([subQ0,subQ1]),TDD([makeQuery(id+"F2.imprint","INTERSECT",VERTEX,{"disambiguationData":[OD(0.0)],"derivedFrom":[makeQuery(id+"F1.opExtrude","CAP_EDGE",EDGE,{"disambiguationData":[OSD([subQ0])],"isStart":false}),subQ1]})])]})})});}
            var Q76;
            {var subQ0=sQuery(id+"F0.wireOp",EDGE,"E0.bottom");var subQ1=sQuery(id+"F2.wireOp",EDGE,"E2");Q76=makeQuery(id+"F5.boolean.opBoolean","SPLIT",EDGE,{"disambiguationData":[TD([makeQuery(id+"F5.opExtrude","SWEPT_FACE",FACE,{"disambiguationData":[OSD([sQuery(id+"F4.wireOp",EDGE,"E6.top")])]})])],"derivedFrom":makeQuery(id+"F3.boolean.opBoolean","COPY",EDGE,{"derivedFrom":makeQuery(id+"F3.opExtrude","SWEPT_EDGE",EDGE,{"disambiguationData":[OSD([subQ0,subQ1]),TDD([makeQuery(id+"F2.imprint","INTERSECT",VERTEX,{"disambiguationData":[OD(1.0)],"derivedFrom":[makeQuery(id+"F1.opExtrude","CAP_EDGE",EDGE,{"disambiguationData":[OSD([subQ0])],"isStart":false}),subQ1]})])]})})});}
            var Q77;
            {var subQ0=sQuery(id+"F0.wireOp",EDGE,"E0.bottom");var subQ1=sQuery(id+"F2.wireOp",EDGE,"E2");Q77=makeQuery(id+"F5.boolean.opBoolean","SPLIT",EDGE,{"disambiguationData":[TD([makeQuery(id+"F5.opExtrude","SWEPT_FACE",FACE,{"disambiguationData":[OSD([sQuery(id+"F4.wireOp",EDGE,"E6.bottom")])]})])],"derivedFrom":makeQuery(id+"F3.boolean.opBoolean","COPY",EDGE,{"derivedFrom":makeQuery(id+"F3.opExtrude","SWEPT_EDGE",EDGE,{"disambiguationData":[OSD([subQ0,subQ1]),TDD([makeQuery(id+"F2.imprint","INTERSECT",VERTEX,{"disambiguationData":[OD(1.0)],"derivedFrom":[makeQuery(id+"F1.opExtrude","CAP_EDGE",EDGE,{"disambiguationData":[OSD([subQ0])],"isStart":false}),subQ1]})])]})})});}
            var Q78;
            {var subQ0=sQuery(id+"F0.wireOp",EDGE,"E0.bottom");var subQ1=sQuery(id+"F0.wireOp",EDGE,"E0.left");Q78=makeQuery(id+"F5.boolean.opBoolean","SPLIT",EDGE,{"disambiguationData":[TD([makeQuery(id+"F1.opExtrude","SWEPT_FACE",FACE,{"disambiguationData":[OSD([subQ0])]})])],"derivedFrom":makeQuery(id+"F1.opExtrude","CAP_EDGE",EDGE,{"disambiguationData":[OSD([subQ1])],"isStart":false})});}
            var Q79;
            {var subQ0=sQuery(id+"F0.wireOp",EDGE,"E0.left");var subQ1=sQuery(id+"F0.wireOp",EDGE,"E0.top");Q79=makeQuery(id+"F5.boolean.opBoolean","SPLIT",EDGE,{"disambiguationData":[TD([makeQuery(id+"F1.opExtrude","SWEPT_FACE",FACE,{"disambiguationData":[OSD([subQ1])]})])],"derivedFrom":makeQuery(id+"F1.opExtrude","CAP_EDGE",EDGE,{"disambiguationData":[OSD([subQ0])],"isStart":false})});}
            var Q80;
            {var subQ0=sQuery(id+"F0.wireOp",EDGE,"E0.bottom");var subQ1=sQuery(id+"F0.wireOp",EDGE,"E0.right");Q80=makeQuery(id+"F5.boolean.opBoolean","SPLIT",EDGE,{"disambiguationData":[TD([makeQuery(id+"F1.opExtrude","SWEPT_FACE",FACE,{"disambiguationData":[OSD([subQ0])]})])],"derivedFrom":makeQuery(id+"F1.opExtrude","CAP_EDGE",EDGE,{"disambiguationData":[OSD([subQ1])],"isStart":false})});}
            var Q81;
            {var subQ0=sQuery(id+"F0.wireOp",EDGE,"E0.right");var subQ1=sQuery(id+"F0.wireOp",EDGE,"E0.top");Q81=makeQuery(id+"F5.boolean.opBoolean","SPLIT",EDGE,{"disambiguationData":[TD([makeQuery(id+"F1.opExtrude","SWEPT_FACE",FACE,{"disambiguationData":[OSD([subQ1])]})])],"derivedFrom":makeQuery(id+"F1.opExtrude","CAP_EDGE",EDGE,{"disambiguationData":[OSD([subQ0])],"isStart":false})});}
            var Q82;
            {var subQ0=sQuery(id+"F0.wireOp",EDGE,"E0.bottom");var subQ1=sQuery(id+"F2.wireOp",EDGE,"E1");Q82=makeQuery(id+"F5.boolean.opBoolean","SPLIT",EDGE,{"disambiguationData":[TD([makeQuery(id+"F5.opExtrude","SWEPT_FACE",FACE,{"disambiguationData":[OSD([sQuery(id+"F4.wireOp",EDGE,"E6.top")])]})])],"derivedFrom":makeQuery(id+"F3.boolean.opBoolean","COPY",EDGE,{"derivedFrom":makeQuery(id+"F3.opExtrude","SWEPT_EDGE",EDGE,{"disambiguationData":[OSD([subQ0,subQ1]),TDD([makeQuery(id+"F2.imprint","INTERSECT",VERTEX,{"disambiguationData":[OD(0.0)],"derivedFrom":[makeQuery(id+"F1.opExtrude","CAP_EDGE",EDGE,{"disambiguationData":[OSD([subQ0])],"isStart":false}),subQ1]})])]})})});}
            var Q83;
            {var subQ0=sQuery(id+"F0.wireOp",EDGE,"E0.bottom");var subQ1=sQuery(id+"F2.wireOp",EDGE,"E1");Q83=makeQuery(id+"F5.boolean.opBoolean","SPLIT",EDGE,{"disambiguationData":[TD([makeQuery(id+"F5.opExtrude","SWEPT_FACE",FACE,{"disambiguationData":[OSD([sQuery(id+"F4.wireOp",EDGE,"E6.bottom")])]})])],"derivedFrom":makeQuery(id+"F3.boolean.opBoolean","COPY",EDGE,{"derivedFrom":makeQuery(id+"F3.opExtrude","SWEPT_EDGE",EDGE,{"disambiguationData":[OSD([subQ0,subQ1]),TDD([makeQuery(id+"F2.imprint","INTERSECT",VERTEX,{"disambiguationData":[OD(0.0)],"derivedFrom":[makeQuery(id+"F1.opExtrude","CAP_EDGE",EDGE,{"disambiguationData":[OSD([subQ0])],"isStart":false}),subQ1]})])]})})});}
            var Q84;
            {var subQ0=sQuery(id+"F0.wireOp",EDGE,"E0.bottom");var subQ1=sQuery(id+"F2.wireOp",EDGE,"E1");Q84=makeQuery(id+"F5.boolean.opBoolean","SPLIT",EDGE,{"disambiguationData":[TD([makeQuery(id+"F5.opExtrude","SWEPT_FACE",FACE,{"disambiguationData":[OSD([sQuery(id+"F4.wireOp",EDGE,"E6.top")])]})])],"derivedFrom":makeQuery(id+"F3.boolean.opBoolean","COPY",EDGE,{"derivedFrom":makeQuery(id+"F3.opExtrude","SWEPT_EDGE",EDGE,{"disambiguationData":[OSD([subQ0,subQ1]),TDD([makeQuery(id+"F2.imprint","INTERSECT",VERTEX,{"disambiguationData":[OD(1.0)],"derivedFrom":[makeQuery(id+"F1.opExtrude","CAP_EDGE",EDGE,{"disambiguationData":[OSD([subQ0])],"isStart":false}),subQ1]})])]})})});}
            var Q85;
            Q85=makeQuery(id+"F5.boolean.opBoolean","COPY",EDGE,{"disambiguationData":[OD(3.0)],"derivedFrom":makeQuery(id+"F5.opExtrude","CAP_EDGE",EDGE,{"disambiguationData":[OSD([sQuery(id+"F4.wireOp",EDGE,"E6.bottom")])],"isStart":false})});
            var Q86;
            Q86=makeQuery(id+"F5.boolean.opBoolean","INTERSECT",EDGE,{"disambiguationData":[OD(0.0)],"derivedFrom":[makeQuery(id+"F3.boolean.opBoolean","COPY",FACE,{"derivedFrom":makeQuery(id+"F3.opExtrude","SWEPT_FACE",FACE,{"disambiguationData":[OSD([sQuery(id+"F2.wireOp",EDGE,"E3")])]})}),makeQuery(id+"F5.opExtrude","SWEPT_FACE",FACE,{"disambiguationData":[OSD([sQuery(id+"F4.wireOp",EDGE,"E6.top")])]})]});
            var Q87;
            {var subQ0=sQuery(id+"F0.wireOp",EDGE,"E0.bottom");var subQ1=sQuery(id+"F2.wireOp",EDGE,"E1");Q87=makeQuery(id+"F5.boolean.opBoolean","SPLIT",EDGE,{"disambiguationData":[TD([makeQuery(id+"F5.opExtrude","SWEPT_FACE",FACE,{"disambiguationData":[OSD([sQuery(id+"F4.wireOp",EDGE,"E6.bottom")])]})])],"derivedFrom":makeQuery(id+"F3.boolean.opBoolean","COPY",EDGE,{"derivedFrom":makeQuery(id+"F3.opExtrude","SWEPT_EDGE",EDGE,{"disambiguationData":[OSD([subQ0,subQ1]),TDD([makeQuery(id+"F2.imprint","INTERSECT",VERTEX,{"disambiguationData":[OD(1.0)],"derivedFrom":[makeQuery(id+"F1.opExtrude","CAP_EDGE",EDGE,{"disambiguationData":[OSD([subQ0])],"isStart":false}),subQ1]})])]})})});}
            var Q88;
            {var subQ0=sQuery(id+"F0.wireOp",EDGE,"E0.bottom");var subQ1=sQuery(id+"F2.wireOp",EDGE,"E4");Q88=makeQuery(id+"F5.boolean.opBoolean","SPLIT",EDGE,{"disambiguationData":[TD([makeQuery(id+"F5.opExtrude","SWEPT_FACE",FACE,{"disambiguationData":[OSD([sQuery(id+"F4.wireOp",EDGE,"E6.top")])]})])],"derivedFrom":makeQuery(id+"F3.boolean.opBoolean","COPY",EDGE,{"derivedFrom":makeQuery(id+"F3.opExtrude","SWEPT_EDGE",EDGE,{"disambiguationData":[OSD([subQ0,subQ1]),TDD([makeQuery(id+"F2.imprint","INTERSECT",VERTEX,{"disambiguationData":[OD(0.0)],"derivedFrom":[makeQuery(id+"F1.opExtrude","CAP_EDGE",EDGE,{"disambiguationData":[OSD([subQ0])],"isStart":false}),subQ1]})])]})})});}
            var Q89;
            Q89=makeQuery(id+"F5.boolean.opBoolean","COPY",FACE,{"disambiguationData":[OD(0.0)],"derivedFrom":makeQuery(id+"F5.opExtrude","SWEPT_FACE",FACE,{"disambiguationData":[OSD([sQuery(id+"F4.wireOp",EDGE,"E6.bottom")])]})});
            var Q90;
            {var subQ0=sQuery(id+"F0.wireOp",EDGE,"E0.bottom");var subQ1=sQuery(id+"F2.wireOp",EDGE,"E4");Q90=makeQuery(id+"F5.boolean.opBoolean","SPLIT",EDGE,{"disambiguationData":[TD([makeQuery(id+"F5.opExtrude","SWEPT_FACE",FACE,{"disambiguationData":[OSD([sQuery(id+"F4.wireOp",EDGE,"E6.bottom")])]})])],"derivedFrom":makeQuery(id+"F3.boolean.opBoolean","COPY",EDGE,{"derivedFrom":makeQuery(id+"F3.opExtrude","SWEPT_EDGE",EDGE,{"disambiguationData":[OSD([subQ0,subQ1]),TDD([makeQuery(id+"F2.imprint","INTERSECT",VERTEX,{"disambiguationData":[OD(0.0)],"derivedFrom":[makeQuery(id+"F1.opExtrude","CAP_EDGE",EDGE,{"disambiguationData":[OSD([subQ0])],"isStart":false}),subQ1]})])]})})});}
            var Q91;
            Q91=makeQuery(id+"F5.boolean.opBoolean","COPY",FACE,{"disambiguationData":[OD(2.0)],"derivedFrom":makeQuery(id+"F5.opExtrude","SWEPT_FACE",FACE,{"disambiguationData":[OSD([sQuery(id+"F4.wireOp",EDGE,"E6.bottom")])]})});
            var Q92;
            {var subQ0=sQuery(id+"F0.wireOp",EDGE,"E0.bottom");var subQ1=sQuery(id+"F2.wireOp",EDGE,"E4");Q92=makeQuery(id+"F5.boolean.opBoolean","SPLIT",EDGE,{"disambiguationData":[TD([makeQuery(id+"F5.opExtrude","SWEPT_FACE",FACE,{"disambiguationData":[OSD([sQuery(id+"F4.wireOp",EDGE,"E6.top")])]})])],"derivedFrom":makeQuery(id+"F3.boolean.opBoolean","COPY",EDGE,{"derivedFrom":makeQuery(id+"F3.opExtrude","SWEPT_EDGE",EDGE,{"disambiguationData":[OSD([subQ0,subQ1]),TDD([makeQuery(id+"F2.imprint","INTERSECT",VERTEX,{"disambiguationData":[OD(1.0)],"derivedFrom":[makeQuery(id+"F1.opExtrude","CAP_EDGE",EDGE,{"disambiguationData":[OSD([subQ0])],"isStart":false}),subQ1]})])]})})});}
            var Q93;
            {var subQ0=sQuery(id+"F0.wireOp",EDGE,"E0.bottom");var subQ1=sQuery(id+"F2.wireOp",EDGE,"E4");Q93=makeQuery(id+"F5.boolean.opBoolean","SPLIT",EDGE,{"disambiguationData":[TD([makeQuery(id+"F5.opExtrude","SWEPT_FACE",FACE,{"disambiguationData":[OSD([sQuery(id+"F4.wireOp",EDGE,"E6.bottom")])]})])],"derivedFrom":makeQuery(id+"F3.boolean.opBoolean","COPY",EDGE,{"derivedFrom":makeQuery(id+"F3.opExtrude","SWEPT_EDGE",EDGE,{"disambiguationData":[OSD([subQ0,subQ1]),TDD([makeQuery(id+"F2.imprint","INTERSECT",VERTEX,{"disambiguationData":[OD(1.0)],"derivedFrom":[makeQuery(id+"F1.opExtrude","CAP_EDGE",EDGE,{"disambiguationData":[OSD([subQ0])],"isStart":false}),subQ1]})])]})})});}
            var Q94;
            Q94=makeQuery(id+"F5.boolean.opBoolean","COPY",FACE,{"disambiguationData":[OD(4.0)],"derivedFrom":makeQuery(id+"F5.opExtrude","SWEPT_FACE",FACE,{"disambiguationData":[OSD([sQuery(id+"F4.wireOp",EDGE,"E6.bottom")])]})});
            var Q95;
            {var subQ0=sQuery(id+"F0.wireOp",EDGE,"E0.bottom");var subQ1=sQuery(id+"F2.wireOp",EDGE,"E2");Q95=makeQuery(id+"F5.boolean.opBoolean","SPLIT",EDGE,{"disambiguationData":[TD([makeQuery(id+"F5.opExtrude","SWEPT_FACE",FACE,{"disambiguationData":[OSD([sQuery(id+"F4.wireOp",EDGE,"E6.top")])]})])],"derivedFrom":makeQuery(id+"F3.boolean.opBoolean","COPY",EDGE,{"derivedFrom":makeQuery(id+"F3.opExtrude","SWEPT_EDGE",EDGE,{"disambiguationData":[OSD([subQ0,subQ1]),TDD([makeQuery(id+"F2.imprint","INTERSECT",VERTEX,{"disambiguationData":[OD(0.0)],"derivedFrom":[makeQuery(id+"F1.opExtrude","CAP_EDGE",EDGE,{"disambiguationData":[OSD([subQ0])],"isStart":false}),subQ1]})])]})})});}
            var Q96;
            Q96=makeQuery(id+"F5.boolean.opBoolean","INTERSECT",EDGE,{"disambiguationData":[OD(1.0)],"derivedFrom":[makeQuery(id+"F3.boolean.opBoolean","COPY",FACE,{"derivedFrom":makeQuery(id+"F3.opExtrude","SWEPT_FACE",FACE,{"disambiguationData":[OSD([sQuery(id+"F2.wireOp",EDGE,"E2")])]})}),makeQuery(id+"F5.opExtrude","CAP_FACE",FACE,{"disambiguationData":[OSD([sQuery(id+"F4.wireOp",EDGE,"E6.bottom"),sQuery(id+"F4.wireOp",EDGE,"E6.top"),sQuery(id+"F4.wireOp",EDGE,"E6.left"),sQuery(id+"F4.wireOp",EDGE,"E6.right")])],"isStart":false})]});
            var Q97;
            {var subQ0=sQuery(id+"F0.wireOp",EDGE,"E0.bottom");var subQ1=sQuery(id+"F2.wireOp",EDGE,"E3");Q97=makeQuery(id+"F5.boolean.opBoolean","SPLIT",EDGE,{"disambiguationData":[TD([makeQuery(id+"F5.opExtrude","SWEPT_FACE",FACE,{"disambiguationData":[OSD([sQuery(id+"F4.wireOp",EDGE,"E6.bottom")])]})])],"derivedFrom":makeQuery(id+"F3.boolean.opBoolean","COPY",EDGE,{"derivedFrom":makeQuery(id+"F3.opExtrude","SWEPT_EDGE",EDGE,{"disambiguationData":[OSD([subQ0,subQ1]),TDD([makeQuery(id+"F2.imprint","INTERSECT",VERTEX,{"disambiguationData":[OD(1.0)],"derivedFrom":[makeQuery(id+"F1.opExtrude","CAP_EDGE",EDGE,{"disambiguationData":[OSD([subQ0])],"isStart":false}),subQ1]})])]})})});}
            var Q98;
            {var subQ0=sQuery(id+"F2.wireOp",EDGE,"E3");var subQ1=sQuery(id+"F0.wireOp",EDGE,"E0.bottom");var subQ2=makeQuery(id+"F1.opExtrude","CAP_EDGE",EDGE,{"disambiguationData":[OSD([subQ1])],"isStart":false});Q98=makeQuery(id+"F3.boolean.opBoolean","COPY",EDGE,{"derivedFrom":makeQuery(id+"F3.opExtrude","CAP_EDGE",EDGE,{"disambiguationData":[OSD([subQ1]),TDD([makeQuery(id+"F2.imprint","IMPRINT",EDGE,{"disambiguationData":[TD([[makeQuery(id+"F2.imprint","INTERSECT",VERTEX,{"disambiguationData":[OD(0.0)],"derivedFrom":[subQ2,subQ0]}),1.0]])],"derivedFrom":subQ2})])],"isStart":true})});}
            var Q99;
            Q99=makeQuery(id+"F3.boolean.opBoolean","COPY",EDGE,{"derivedFrom":makeQuery(id+"F3.opExtrude","CAP_EDGE",EDGE,{"disambiguationData":[OSD([sQuery(id+"F2.wireOp",EDGE,"E2")])],"isStart":true})});
            var Q100;
            Q100=makeQuery(id+"F3.boolean.opBoolean","COPY",EDGE,{"derivedFrom":makeQuery(id+"F3.opExtrude","CAP_EDGE",EDGE,{"disambiguationData":[OSD([sQuery(id+"F2.wireOp",EDGE,"E1")])],"isStart":false})});
            var Q101;
            Q101=makeQuery(id+"F5.boolean.opBoolean","INTERSECT",EDGE,{"disambiguationData":[OD(0.0)],"derivedFrom":[makeQuery(id+"F3.boolean.opBoolean","COPY",FACE,{"derivedFrom":makeQuery(id+"F3.opExtrude","SWEPT_FACE",FACE,{"disambiguationData":[OSD([sQuery(id+"F2.wireOp",EDGE,"E4")])]})}),makeQuery(id+"F5.opExtrude","SWEPT_FACE",FACE,{"disambiguationData":[OSD([sQuery(id+"F4.wireOp",EDGE,"E6.top")])]})]});
            var Q102;
            {var subQ0=sQuery(id+"F0.wireOp",EDGE,"E0.bottom");var subQ1=sQuery(id+"F2.wireOp",EDGE,"E3");Q102=makeQuery(id+"F5.boolean.opBoolean","SPLIT",EDGE,{"disambiguationData":[TD([makeQuery(id+"F5.opExtrude","SWEPT_FACE",FACE,{"disambiguationData":[OSD([sQuery(id+"F4.wireOp",EDGE,"E6.top")])]})])],"derivedFrom":makeQuery(id+"F3.boolean.opBoolean","COPY",EDGE,{"derivedFrom":makeQuery(id+"F3.opExtrude","SWEPT_EDGE",EDGE,{"disambiguationData":[OSD([subQ0,subQ1]),TDD([makeQuery(id+"F2.imprint","INTERSECT",VERTEX,{"disambiguationData":[OD(0.0)],"derivedFrom":[makeQuery(id+"F1.opExtrude","CAP_EDGE",EDGE,{"disambiguationData":[OSD([subQ0])],"isStart":false}),subQ1]})])]})})});}
            var Q103;
            Q103=makeQuery(id+"F5.boolean.opBoolean","COPY",EDGE,{"disambiguationData":[OD(4.0)],"derivedFrom":makeQuery(id+"F5.opExtrude","CAP_EDGE",EDGE,{"disambiguationData":[OSD([sQuery(id+"F4.wireOp",EDGE,"E6.top")])],"isStart":true})});
            var Q104;
            Q104=makeQuery(id+"F3.boolean.opBoolean","COPY",FACE,{"derivedFrom":makeQuery(id+"F3.opExtrude","CAP_FACE",FACE,{"disambiguationData":[OSD([sQuery(id+"F0.wireOp",EDGE,"E0.bottom"),sQuery(id+"F2.wireOp",EDGE,"E1")])],"isStart":true})});
            var Q105;
            Q105=makeQuery(id+"F3.boolean.opBoolean","COPY",EDGE,{"derivedFrom":makeQuery(id+"F3.opExtrude","CAP_EDGE",EDGE,{"disambiguationData":[OSD([sQuery(id+"F2.wireOp",EDGE,"E4")])],"isStart":false})});
            var Q106;
            Q106=makeQuery(id+"F3.boolean.opBoolean","COPY",EDGE,{"derivedFrom":makeQuery(id+"F3.opExtrude","CAP_EDGE",EDGE,{"disambiguationData":[OSD([sQuery(id+"F2.wireOp",EDGE,"E3")])],"isStart":false})});
            var Q107;
            Q107=makeQuery(id+"F3.boolean.opBoolean","COPY",EDGE,{"derivedFrom":makeQuery(id+"F3.opExtrude","CAP_EDGE",EDGE,{"disambiguationData":[OSD([sQuery(id+"F2.wireOp",EDGE,"E4")])],"isStart":true})});
            var Q108;
            Q108=makeQuery(id+"F5.boolean.opBoolean","INTERSECT",EDGE,{"disambiguationData":[OD(1.0)],"derivedFrom":[makeQuery(id+"F3.boolean.opBoolean","COPY",FACE,{"derivedFrom":makeQuery(id+"F3.opExtrude","SWEPT_FACE",FACE,{"disambiguationData":[OSD([sQuery(id+"F2.wireOp",EDGE,"E3")])]})}),makeQuery(id+"F5.opExtrude","SWEPT_FACE",FACE,{"disambiguationData":[OSD([sQuery(id+"F4.wireOp",EDGE,"E6.top")])]})]});
            var Q109;
            {var subQ0=sQuery(id+"F2.wireOp",EDGE,"E2");var subQ1=sQuery(id+"F0.wireOp",EDGE,"E0.bottom");var subQ2=makeQuery(id+"F1.opExtrude","CAP_EDGE",EDGE,{"disambiguationData":[OSD([subQ1])],"isStart":false});Q109=makeQuery(id+"F3.boolean.opBoolean","COPY",EDGE,{"derivedFrom":makeQuery(id+"F3.opExtrude","CAP_EDGE",EDGE,{"disambiguationData":[OSD([subQ1]),TDD([makeQuery(id+"F2.imprint","IMPRINT",EDGE,{"disambiguationData":[TD([[makeQuery(id+"F2.imprint","INTERSECT",VERTEX,{"disambiguationData":[OD(0.0)],"derivedFrom":[subQ2,subQ0]}),-1.0]])],"derivedFrom":subQ2})])],"isStart":false})});}
            var Q110;
            Q110=makeQuery(id+"F1.opExtrude","CAP_EDGE",EDGE,{"disambiguationData":[OSD([sQuery(id+"F0.wireOp",EDGE,"E0.right")])],"isStart":true});
            var Q111;
            Q111=makeQuery(id+"F1.opExtrude","CAP_EDGE",EDGE,{"disambiguationData":[OSD([sQuery(id+"F0.wireOp",EDGE,"E0.left")])],"isStart":true});
            var Q112;
            Q112=makeQuery(id+"F1.opExtrude","CAP_EDGE",EDGE,{"disambiguationData":[OSD([sQuery(id+"F0.wireOp",EDGE,"E0.bottom")])],"isStart":true});
            var Q113;
            Q113=makeQuery(id+"F1.opExtrude","SWEPT_EDGE",EDGE,{"disambiguationData":[OSD([sQuery(id+"F0.wireOp",EDGE,"E0.bottom"),sQuery(id+"F0.wireOp",EDGE,"E0.left")])]});
            var Q114;
            {var subQ0=sQuery(id+"F2.wireOp",EDGE,"E1");var subQ1=sQuery(id+"F0.wireOp",EDGE,"E0.bottom");var subQ2=makeQuery(id+"F1.opExtrude","CAP_EDGE",EDGE,{"disambiguationData":[OSD([subQ1])],"isStart":false});Q114=makeQuery(id+"F3.boolean.opBoolean","COPY",EDGE,{"derivedFrom":makeQuery(id+"F3.opExtrude","CAP_EDGE",EDGE,{"disambiguationData":[OSD([subQ1]),TDD([makeQuery(id+"F2.imprint","IMPRINT",EDGE,{"disambiguationData":[TD([[makeQuery(id+"F2.imprint","INTERSECT",VERTEX,{"disambiguationData":[OD(0.0)],"derivedFrom":[subQ2,subQ0]}),-1.0]])],"derivedFrom":subQ2})])],"isStart":false})});}
            var Q115;
            {var subQ0=sQuery(id+"F2.wireOp",EDGE,"E4");var subQ1=sQuery(id+"F0.wireOp",EDGE,"E0.bottom");var subQ2=makeQuery(id+"F1.opExtrude","CAP_EDGE",EDGE,{"disambiguationData":[OSD([subQ1])],"isStart":false});Q115=makeQuery(id+"F3.boolean.opBoolean","COPY",EDGE,{"derivedFrom":makeQuery(id+"F3.opExtrude","CAP_EDGE",EDGE,{"disambiguationData":[OSD([subQ1]),TDD([makeQuery(id+"F2.imprint","IMPRINT",EDGE,{"disambiguationData":[TD([[makeQuery(id+"F2.imprint","INTERSECT",VERTEX,{"disambiguationData":[OD(0.0)],"derivedFrom":[subQ2,subQ0]}),1.0]])],"derivedFrom":subQ2})])],"isStart":false})});}
            var Q116;
            {var subQ0=sQuery(id+"F2.wireOp",EDGE,"E1");var subQ1=sQuery(id+"F0.wireOp",EDGE,"E0.bottom");var subQ2=makeQuery(id+"F1.opExtrude","CAP_EDGE",EDGE,{"disambiguationData":[OSD([subQ1])],"isStart":false});Q116=makeQuery(id+"F3.boolean.opBoolean","COPY",EDGE,{"derivedFrom":makeQuery(id+"F3.opExtrude","CAP_EDGE",EDGE,{"disambiguationData":[OSD([subQ1]),TDD([makeQuery(id+"F2.imprint","IMPRINT",EDGE,{"disambiguationData":[TD([[makeQuery(id+"F2.imprint","INTERSECT",VERTEX,{"disambiguationData":[OD(0.0)],"derivedFrom":[subQ2,subQ0]}),-1.0]])],"derivedFrom":subQ2})])],"isStart":true})});}
            var Q117;
            {var subQ0=sQuery(id+"F2.wireOp",EDGE,"E4");var subQ1=sQuery(id+"F0.wireOp",EDGE,"E0.bottom");var subQ2=makeQuery(id+"F1.opExtrude","CAP_EDGE",EDGE,{"disambiguationData":[OSD([subQ1])],"isStart":false});Q117=makeQuery(id+"F3.boolean.opBoolean","COPY",EDGE,{"derivedFrom":makeQuery(id+"F3.opExtrude","CAP_EDGE",EDGE,{"disambiguationData":[OSD([subQ1]),TDD([makeQuery(id+"F2.imprint","IMPRINT",EDGE,{"disambiguationData":[TD([[makeQuery(id+"F2.imprint","INTERSECT",VERTEX,{"disambiguationData":[OD(0.0)],"derivedFrom":[subQ2,subQ0]}),1.0]])],"derivedFrom":subQ2})])],"isStart":true})});}
            var Q118;
            Q118=makeQuery(id+"F5.boolean.opBoolean","COPY",EDGE,{"disambiguationData":[OD(0.0)],"derivedFrom":makeQuery(id+"F5.opExtrude","CAP_EDGE",EDGE,{"disambiguationData":[OSD([sQuery(id+"F4.wireOp",EDGE,"E6.bottom")])],"isStart":false})});
            var Q119;
            Q119=makeQuery(id+"F5.boolean.opBoolean","INTERSECT",EDGE,{"disambiguationData":[OD(1.0)],"derivedFrom":[makeQuery(id+"F3.boolean.opBoolean","COPY",FACE,{"derivedFrom":makeQuery(id+"F3.opExtrude","SWEPT_FACE",FACE,{"disambiguationData":[OSD([sQuery(id+"F2.wireOp",EDGE,"E4")])]})}),makeQuery(id+"F5.opExtrude","SWEPT_FACE",FACE,{"disambiguationData":[OSD([sQuery(id+"F4.wireOp",EDGE,"E6.bottom")])]})]});
            var Q120;
            Q120=makeQuery(id+"F5.boolean.opBoolean","INTERSECT",EDGE,{"disambiguationData":[OD(1.0)],"derivedFrom":[makeQuery(id+"F3.boolean.opBoolean","COPY",FACE,{"derivedFrom":makeQuery(id+"F3.opExtrude","SWEPT_FACE",FACE,{"disambiguationData":[OSD([sQuery(id+"F2.wireOp",EDGE,"E3")])]})}),makeQuery(id+"F5.opExtrude","SWEPT_FACE",FACE,{"disambiguationData":[OSD([sQuery(id+"F4.wireOp",EDGE,"E6.bottom")])]})]});
            var Q121;
            Q121=makeQuery(id+"F5.boolean.opBoolean","COPY",EDGE,{"disambiguationData":[OD(4.0)],"derivedFrom":makeQuery(id+"F5.opExtrude","CAP_EDGE",EDGE,{"disambiguationData":[OSD([sQuery(id+"F4.wireOp",EDGE,"E6.bottom")])],"isStart":true})});
            var Q122;
            Q122=makeQuery(id+"F5.boolean.opBoolean","COPY",EDGE,{"disambiguationData":[OD(0.0)],"derivedFrom":makeQuery(id+"F5.opExtrude","CAP_EDGE",EDGE,{"disambiguationData":[OSD([sQuery(id+"F4.wireOp",EDGE,"E6.bottom")])],"isStart":true})});
            var Q123;
            Q123=makeQuery(id+"F5.boolean.opBoolean","INTERSECT",EDGE,{"disambiguationData":[OD(0.0)],"derivedFrom":[makeQuery(id+"F3.boolean.opBoolean","COPY",FACE,{"derivedFrom":makeQuery(id+"F3.opExtrude","SWEPT_FACE",FACE,{"disambiguationData":[OSD([sQuery(id+"F2.wireOp",EDGE,"E1")])]})}),makeQuery(id+"F5.opExtrude","SWEPT_FACE",FACE,{"disambiguationData":[OSD([sQuery(id+"F4.wireOp",EDGE,"E6.bottom")])]})]});
            var Q124;
            Q124=makeQuery(id+"F5.boolean.opBoolean","COPY",EDGE,{"disambiguationData":[OD(1.0)],"derivedFrom":makeQuery(id+"F5.opExtrude","CAP_EDGE",EDGE,{"disambiguationData":[OSD([sQuery(id+"F4.wireOp",EDGE,"E6.bottom")])],"isStart":true})});
            var Q125;
            Q125=makeQuery(id+"F3.boolean.opBoolean","COPY",EDGE,{"derivedFrom":makeQuery(id+"F3.opExtrude","CAP_EDGE",EDGE,{"disambiguationData":[OSD([sQuery(id+"F2.wireOp",EDGE,"E1")])],"isStart":true})});
            var Q126;
            Q126=makeQuery(id+"F5.boolean.opBoolean","INTERSECT",EDGE,{"disambiguationData":[OD(0.0)],"derivedFrom":[makeQuery(id+"F3.boolean.opBoolean","COPY",FACE,{"derivedFrom":makeQuery(id+"F3.opExtrude","SWEPT_FACE",FACE,{"disambiguationData":[OSD([sQuery(id+"F2.wireOp",EDGE,"E2")])]})}),makeQuery(id+"F5.opExtrude","SWEPT_FACE",FACE,{"disambiguationData":[OSD([sQuery(id+"F4.wireOp",EDGE,"E6.bottom")])]})]});
            var Q127;
            Q127=makeQuery(id+"F5.boolean.opBoolean","INTERSECT",EDGE,{"disambiguationData":[OD(1.0)],"derivedFrom":[makeQuery(id+"F3.boolean.opBoolean","COPY",FACE,{"derivedFrom":makeQuery(id+"F3.opExtrude","SWEPT_FACE",FACE,{"disambiguationData":[OSD([sQuery(id+"F2.wireOp",EDGE,"E1")])]})}),makeQuery(id+"F5.opExtrude","SWEPT_FACE",FACE,{"disambiguationData":[OSD([sQuery(id+"F4.wireOp",EDGE,"E6.bottom")])]})]});
            var Q128;
            Q128=makeQuery(id+"F5.boolean.opBoolean","COPY",EDGE,{"disambiguationData":[OD(4.0)],"derivedFrom":makeQuery(id+"F5.opExtrude","CAP_EDGE",EDGE,{"disambiguationData":[OSD([sQuery(id+"F4.wireOp",EDGE,"E6.bottom")])],"isStart":false})});
            var Q129;
            Q129=makeQuery(id+"F5.boolean.opBoolean","COPY",EDGE,{"disambiguationData":[OD(2.0)],"derivedFrom":makeQuery(id+"F5.opExtrude","CAP_EDGE",EDGE,{"disambiguationData":[OSD([sQuery(id+"F4.wireOp",EDGE,"E6.bottom")])],"isStart":true})});
            fillet(context, id + "F6", {"entities" : qUnion([Q0, Q1, Q2, Q3, Q4, Q5, Q6, Q7, Q8, Q9, Q10, Q11, Q12, Q13, Q14, Q15, Q16, Q17, Q18, Q19, Q20, Q21, Q22, Q23, Q24, Q25, Q26, Q27, Q28, Q29, Q30, Q31, Q32, Q33, Q34, Q35, Q36, Q37, Q38, Q39, Q40, Q41, Q42, Q43, Q44, Q45, Q46, Q47, Q48, Q49, Q50, Q51, Q52, Q53, Q54, Q55, Q56, Q57, Q58, Q59, Q60, Q61, Q62, Q63, Q64, Q65, Q66, Q67, Q68, Q69, Q70, Q71, Q72, Q73, Q74, Q75, Q76, Q77, Q78, Q79, Q80, Q81, Q82, Q83, Q84, Q85, Q86, Q87, Q88, Q89, Q90, Q91, Q92, Q93, Q94, Q95, Q96, Q97, Q98, Q99, Q100, Q101, Q102, Q103, Q104, Q105, Q106, Q107, Q108, Q109, Q110, Q111, Q112, Q113, Q114, Q115, Q116, Q117, Q118, Q119, Q120, Q121, Q122, Q123, Q124, Q125, Q126, Q127, Q128, Q129]), "radius" : 1.27 * mm, "tangentPropagation" : true, "allowEdgeOverflow" : false});
        }
    });
